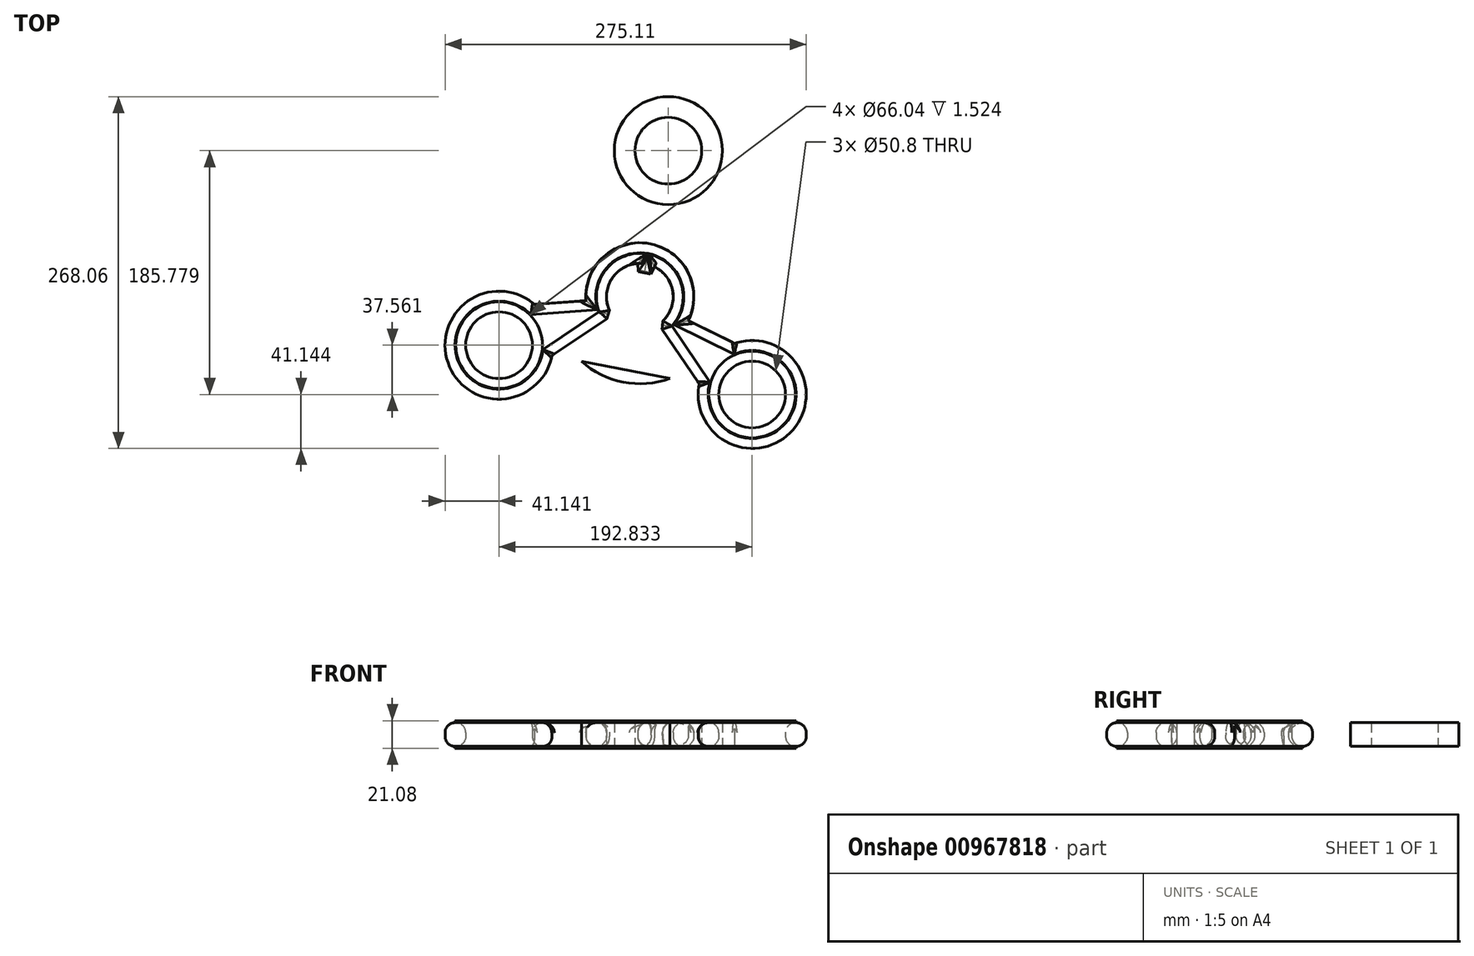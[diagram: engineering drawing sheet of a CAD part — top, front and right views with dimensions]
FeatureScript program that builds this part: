
annotation { "Feature Type Name" : "Feature", "Feature Type Description" : "" }
export const myFeature = defineFeature(function(context is Context, id is Id, definition is map)
    precondition{}
    {
        {
            var Q0;
            Q0=qCreatedBy(makeId("Top.planeOp"),FACE);
            var sketch = newSketch(context, id + "F0", { "sketchPlane" : qUnion([Q0])});
            skCircle(sketch, "E0", {"center": v(0, 0) * mm, "radius": 66.28 * mm});
            skLineSegment(sketch, "E1", {"start": v(0, 66.28) * mm, "end": v(0, -66.28) * mm});
            skCircle(sketch, "E2.cCircle", {"center": v(0, 0) * mm, "radius": 56.71 * mm, "construction": true});
            skLineSegment(sketch, "E2.0", {"start": v(-107.26, -36.89) * mm, "end": v(21.69, 111.33) * mm});
            skLineSegment(sketch, "E2.1", {"start": v(21.69, 111.33) * mm, "end": v(85.57, -74.45) * mm});
            skLineSegment(sketch, "E2.2", {"start": v(85.57, -74.45) * mm, "end": v(-107.26, -36.89) * mm});
            skPoint(sketch, "E2.0.midPoint", {"position": v(-42.79, 37.22) * mm});
            skCircle(sketch, "E3", {"center": v(-107.26, -36.89) * mm, "radius": 41.14 * mm});
            skCircle(sketch, "E4", {"center": v(85.57, -74.45) * mm, "radius": 41.14 * mm});
            skCircle(sketch, "E5", {"center": v(21.69, 111.33) * mm, "radius": 41.14 * mm});
            skCircle(sketch, "E6", {"center": v(0, 0) * mm, "radius": 41.15 * mm});
            skLineSegment(sketch, "E7", {"start": v(0, 0) * mm, "end": v(-5.32, 80.3) * mm});
            skLineSegment(sketch, "E8", {"start": v(-5.32, 80.3) * mm, "end": v(-80.26, -5.85) * mm});
            skLineSegment(sketch, "E9", {"start": v(21.69, 111.33) * mm, "end": v(53.63, 18.44) * mm});
            skLineSegment(sketch, "E10", {"start": v(35.06, 72.43) * mm, "end": v(0, 0) * mm});
            skCircle(sketch, "E11", {"center": v(-107.26, -36.89) * mm, "radius": 25.4 * mm});
            skCircle(sketch, "E12", {"center": v(21.69, 111.33) * mm, "radius": 25.4 * mm});
            skCircle(sketch, "E13", {"center": v(85.57, -74.45) * mm, "radius": 25.4 * mm});
            skLineSegment(sketch, "E14", {"start": v(0, 0) * mm, "end": v(-80.26, -5.85) * mm});
            skLineSegment(sketch, "E15", {"start": v(-66.88, -44.75) * mm, "end": v(0, 0) * mm});
            skLineSegment(sketch, "E16", {"start": v(0, 0) * mm, "end": v(45.2, -66.58) * mm});
            skLineSegment(sketch, "E17", {"start": v(0, 0) * mm, "end": v(72.2, -35.54) * mm});
            skLineSegment(sketch, "E18", {"start": v(-5.32, 80.3) * mm, "end": v(35.06, 72.43) * mm});
            skLineSegment(sketch, "E19", {"start": v(72.2, -35.54) * mm, "end": v(45.2, -66.58) * mm});
            skLineSegment(sketch, "E20", {"start": v(-80.26, -5.85) * mm, "end": v(-66.88, -44.75) * mm});
            skCircle(sketch, "E21", {"center": v(0, 0) * mm, "radius": 25.4 * mm});
            skSolve(sketch);
        }
        {
            var Q0;
            {var subQ0=sQuery(id+"F0.wireOp",EDGE,"E7");var subQ1=sQuery(id+"F0.wireOp",EDGE,"E6");var subQ2=makeQuery(id+"F0.imprint","INTERSECT",VERTEX,{"derivedFrom":[subQ1,subQ0]});Q0=makeQuery(id+"F0.imprint","IMPRINT",FACE,{"disambiguationData":[TD([[makeQuery(id+"F0.imprint","IMPRINT",EDGE,{"disambiguationData":[TD([[subQ2,-1.0]])],"derivedFrom":subQ1}),1.0]])]});}
            var Q1;
            {var subQ0=sQuery(id+"F0.wireOp",EDGE,"E6");var subQ1=sQuery(id+"F0.wireOp",EDGE,"E1");var subQ2=makeQuery(id+"F0.imprint","INTERSECT",VERTEX,{"disambiguationData":[OD(0.0)],"derivedFrom":[subQ1,subQ0]});Q1=makeQuery(id+"F0.imprint","IMPRINT",FACE,{"disambiguationData":[TD([[makeQuery(id+"F0.imprint","IMPRINT",EDGE,{"disambiguationData":[TD([[subQ2,-1.0]])],"derivedFrom":subQ1}),1.0]])]});}
            var Q2;
            {var subQ0=sQuery(id+"F0.wireOp",EDGE,"E10");var subQ1=sQuery(id+"F0.wireOp",EDGE,"E6");var subQ2=makeQuery(id+"F0.imprint","INTERSECT",VERTEX,{"derivedFrom":[subQ1,subQ0]});Q2=makeQuery(id+"F0.imprint","IMPRINT",FACE,{"disambiguationData":[TD([[makeQuery(id+"F0.imprint","IMPRINT",EDGE,{"disambiguationData":[TD([[subQ2,1.0]])],"derivedFrom":subQ1}),1.0]])]});}
            var Q3;
            {var subQ0=sQuery(id+"F0.wireOp",EDGE,"E6");var subQ1=sQuery(id+"F0.wireOp",EDGE,"E1");var subQ2=makeQuery(id+"F0.imprint","INTERSECT",VERTEX,{"disambiguationData":[OD(0.0)],"derivedFrom":[subQ1,subQ0]});Q3=makeQuery(id+"F0.imprint","IMPRINT",FACE,{"disambiguationData":[TD([[makeQuery(id+"F0.imprint","IMPRINT",EDGE,{"disambiguationData":[TD([[subQ2,-1.0]])],"derivedFrom":subQ1}),-1.0]])]});}
            var Q4;
            {var subQ0=sQuery(id+"F0.wireOp",EDGE,"E14");var subQ1=sQuery(id+"F0.wireOp",EDGE,"E6");var subQ2=makeQuery(id+"F0.imprint","INTERSECT",VERTEX,{"derivedFrom":[subQ1,subQ0]});Q4=makeQuery(id+"F0.imprint","IMPRINT",FACE,{"disambiguationData":[TD([[makeQuery(id+"F0.imprint","IMPRINT",EDGE,{"disambiguationData":[TD([[subQ2,-1.0]])],"derivedFrom":subQ1}),1.0]])]});}
            var Q5;
            {var subQ0=sQuery(id+"F0.wireOp",EDGE,"E21");var subQ1=sQuery(id+"F0.wireOp",EDGE,"E1");var subQ2=makeQuery(id+"F0.imprint","INTERSECT",VERTEX,{"disambiguationData":[OD(1.0)],"derivedFrom":[subQ1,subQ0]});Q5=makeQuery(id+"F0.imprint","IMPRINT",FACE,{"disambiguationData":[TD([[makeQuery(id+"F0.imprint","IMPRINT",EDGE,{"disambiguationData":[TD([[subQ2,-1.0]])],"derivedFrom":subQ1}),-1.0]])]});}
            var Q6;
            {var subQ0=sQuery(id+"F0.wireOp",EDGE,"E21");var subQ1=sQuery(id+"F0.wireOp",EDGE,"E1");var subQ2=makeQuery(id+"F0.imprint","INTERSECT",VERTEX,{"disambiguationData":[OD(1.0)],"derivedFrom":[subQ1,subQ0]});Q6=makeQuery(id+"F0.imprint","IMPRINT",FACE,{"disambiguationData":[TD([[makeQuery(id+"F0.imprint","IMPRINT",EDGE,{"disambiguationData":[TD([[subQ2,-1.0]])],"derivedFrom":subQ1}),1.0]])]});}
            var Q7;
            {var subQ0=sQuery(id+"F0.wireOp",EDGE,"E16");var subQ1=sQuery(id+"F0.wireOp",EDGE,"E6");var subQ2=makeQuery(id+"F0.imprint","INTERSECT",VERTEX,{"derivedFrom":[subQ1,subQ0]});Q7=makeQuery(id+"F0.imprint","IMPRINT",FACE,{"disambiguationData":[TD([[makeQuery(id+"F0.imprint","IMPRINT",EDGE,{"disambiguationData":[TD([[subQ2,-1.0]])],"derivedFrom":subQ1}),1.0]])]});}
            var Q8;
            {var subQ0=sQuery(id+"F0.wireOp",EDGE,"E16");var subQ1=sQuery(id+"F0.wireOp",EDGE,"E0");var subQ2=makeQuery(id+"F0.imprint","INTERSECT",VERTEX,{"derivedFrom":[subQ1,subQ0]});Q8=makeQuery(id+"F0.imprint","IMPRINT",FACE,{"disambiguationData":[TD([[makeQuery(id+"F0.imprint","IMPRINT",EDGE,{"disambiguationData":[TD([[subQ2,-1.0]])],"derivedFrom":subQ1}),1.0]])]});}
            var Q9;
            {var subQ0=sQuery(id+"F0.wireOp",EDGE,"E14");var subQ1=sQuery(id+"F0.wireOp",EDGE,"E0");var subQ2=makeQuery(id+"F0.imprint","INTERSECT",VERTEX,{"derivedFrom":[subQ1,subQ0]});Q9=makeQuery(id+"F0.imprint","IMPRINT",FACE,{"disambiguationData":[TD([[makeQuery(id+"F0.imprint","IMPRINT",EDGE,{"disambiguationData":[TD([[subQ2,-1.0]])],"derivedFrom":subQ1}),1.0]])]});}
            var Q10;
            {var subQ0=sQuery(id+"F0.wireOp",EDGE,"E14");var subQ1=sQuery(id+"F0.wireOp",EDGE,"E0");var subQ2=makeQuery(id+"F0.imprint","INTERSECT",VERTEX,{"derivedFrom":[subQ1,subQ0]});Q10=makeQuery(id+"F0.imprint","IMPRINT",FACE,{"disambiguationData":[TD([[makeQuery(id+"F0.imprint","IMPRINT",EDGE,{"disambiguationData":[TD([[subQ2,-1.0]])],"derivedFrom":subQ1}),-1.0]])]});}
            var Q11;
            {var subQ0=sQuery(id+"F0.wireOp",EDGE,"E20");Q11=makeQuery(id+"F0.imprint","IMPRINT",FACE,{"disambiguationData":[TD([[makeQuery(id+"F0.imprint","IMPRINT",EDGE,{"derivedFrom":subQ0}),-1.0]])]});}
            var Q12;
            {var subQ0=sQuery(id+"F0.wireOp",EDGE,"E20");Q12=makeQuery(id+"F0.imprint","IMPRINT",FACE,{"disambiguationData":[TD([[makeQuery(id+"F0.imprint","IMPRINT",EDGE,{"derivedFrom":subQ0}),1.0]])]});}
            var Q13;
            {var subQ2=sQuery(id+"F0.wireOp",EDGE,"E2.0");var subQ4=sQuery(id+"F0.wireOp",EDGE,"E11");var subQ5=makeQuery(id+"F0.imprint","INTERSECT",VERTEX,{"derivedFrom":[subQ2,subQ4]});Q13=makeQuery(id+"F0.imprint","IMPRINT",FACE,{"disambiguationData":[TD([[makeQuery(id+"F0.imprint","IMPRINT",EDGE,{"disambiguationData":[TD([[subQ5,-1.0]])],"derivedFrom":subQ4}),-1.0]])]});}
            var Q14;
            {var subQ0=sQuery(id+"F0.wireOp",EDGE,"E19");Q14=makeQuery(id+"F0.imprint","IMPRINT",FACE,{"disambiguationData":[TD([[makeQuery(id+"F0.imprint","IMPRINT",EDGE,{"derivedFrom":subQ0}),1.0]])]});}
            var Q15;
            {var subQ0=sQuery(id+"F0.wireOp",EDGE,"E16");var subQ1=sQuery(id+"F0.wireOp",EDGE,"E0");var subQ2=makeQuery(id+"F0.imprint","INTERSECT",VERTEX,{"derivedFrom":[subQ1,subQ0]});Q15=makeQuery(id+"F0.imprint","IMPRINT",FACE,{"disambiguationData":[TD([[makeQuery(id+"F0.imprint","IMPRINT",EDGE,{"disambiguationData":[TD([[subQ2,-1.0]])],"derivedFrom":subQ1}),-1.0]])]});}
            var Q16;
            {var subQ2=sQuery(id+"F0.wireOp",EDGE,"E2.1");var subQ4=sQuery(id+"F0.wireOp",EDGE,"E13");var subQ5=makeQuery(id+"F0.imprint","INTERSECT",VERTEX,{"derivedFrom":[subQ2,subQ4]});Q16=makeQuery(id+"F0.imprint","IMPRINT",FACE,{"disambiguationData":[TD([[makeQuery(id+"F0.imprint","IMPRINT",EDGE,{"disambiguationData":[TD([[subQ5,1.0]])],"derivedFrom":subQ4}),-1.0]])]});}
            var Q17;
            {var subQ0=sQuery(id+"F0.wireOp",EDGE,"E19");Q17=makeQuery(id+"F0.imprint","IMPRINT",FACE,{"disambiguationData":[TD([[makeQuery(id+"F0.imprint","IMPRINT",EDGE,{"derivedFrom":subQ0}),-1.0]])]});}
            var Q18;
            {var subQ0=sQuery(id+"F0.wireOp",EDGE,"E1");var subQ1=sQuery(id+"F0.wireOp",EDGE,"E0");var subQ2=makeQuery(id+"F0.imprint","INTERSECT",VERTEX,{"disambiguationData":[OD(0.0)],"derivedFrom":[subQ1,subQ0]});Q18=makeQuery(id+"F0.imprint","IMPRINT",FACE,{"disambiguationData":[TD([[makeQuery(id+"F0.imprint","IMPRINT",EDGE,{"disambiguationData":[TD([[subQ2,1.0]])],"derivedFrom":subQ1}),1.0]])]});}
            var Q19;
            {var subQ0=sQuery(id+"F0.wireOp",EDGE,"E1");var subQ1=sQuery(id+"F0.wireOp",EDGE,"E0");var subQ2=makeQuery(id+"F0.imprint","INTERSECT",VERTEX,{"disambiguationData":[OD(0.0)],"derivedFrom":[subQ1,subQ0]});Q19=makeQuery(id+"F0.imprint","IMPRINT",FACE,{"disambiguationData":[TD([[makeQuery(id+"F0.imprint","IMPRINT",EDGE,{"disambiguationData":[TD([[subQ2,-1.0]])],"derivedFrom":subQ1}),1.0]])]});}
            var Q20;
            {var subQ4=sQuery(id+"F0.wireOp",EDGE,"E0");var subQ6=makeQuery(id+"F0.imprint","INTERSECT",VERTEX,{"disambiguationData":[OD(0.0)],"derivedFrom":[subQ4,sQuery(id+"F0.wireOp",EDGE,"E1")]});Q20=makeQuery(id+"F0.imprint","IMPRINT",FACE,{"disambiguationData":[TD([[makeQuery(id+"F0.imprint","IMPRINT",EDGE,{"disambiguationData":[TD([[subQ6,1.0]])],"derivedFrom":subQ4}),-1.0]])]});}
            var Q21;
            {var subQ0=sQuery(id+"F0.wireOp",EDGE,"E18");Q21=makeQuery(id+"F0.imprint","IMPRINT",FACE,{"disambiguationData":[TD([[makeQuery(id+"F0.imprint","IMPRINT",EDGE,{"derivedFrom":subQ0}),-1.0]])]});}
            var Q22;
            {var subQ2=sQuery(id+"F0.wireOp",EDGE,"E2.0");var subQ4=sQuery(id+"F0.wireOp",EDGE,"E12");var subQ5=makeQuery(id+"F0.imprint","INTERSECT",VERTEX,{"derivedFrom":[subQ2,subQ4]});Q22=makeQuery(id+"F0.imprint","IMPRINT",FACE,{"disambiguationData":[TD([[makeQuery(id+"F0.imprint","IMPRINT",EDGE,{"disambiguationData":[TD([[subQ5,1.0]])],"derivedFrom":subQ4}),-1.0]])]});}
            var Q23;
            {var subQ0=sQuery(id+"F0.wireOp",EDGE,"E18");Q23=makeQuery(id+"F0.imprint","IMPRINT",FACE,{"disambiguationData":[TD([[makeQuery(id+"F0.imprint","IMPRINT",EDGE,{"derivedFrom":subQ0}),1.0]])]});}
            extrude(context, id + "F1", {"entities" : qUnion([Q0, Q1, Q2, Q3, Q4, Q5, Q6, Q7, Q8, Q9, Q10, Q11, Q12, Q13, Q14, Q15, Q16, Q17, Q18, Q19, Q20, Q21, Q22, Q23]), "depth" : 18.03 * mm, "offsetDistance" : 25.4 * mm});
        }
        {
            var Q0;
            Q0=makeQuery(id+"F1.opExtrude","CAP_EDGE",EDGE,{"disambiguationData":[OSD([sQuery(id+"F0.wireOp",EDGE,"E4")])],"isStart":false});
            var Q1;
            Q1=makeQuery(id+"F1.opExtrude","CAP_FACE",FACE,{"disambiguationData":[OSD([sQuery(id+"F0.wireOp",EDGE,"E3"),sQuery(id+"F0.wireOp",EDGE,"E4"),sQuery(id+"F0.wireOp",EDGE,"E5"),sQuery(id+"F0.wireOp",EDGE,"E6"),sQuery(id+"F0.wireOp",EDGE,"E7"),sQuery(id+"F0.wireOp",EDGE,"E10"),sQuery(id+"F0.wireOp",EDGE,"E11"),sQuery(id+"F0.wireOp",EDGE,"E12"),sQuery(id+"F0.wireOp",EDGE,"E13"),sQuery(id+"F0.wireOp",EDGE,"E14"),sQuery(id+"F0.wireOp",EDGE,"E15"),sQuery(id+"F0.wireOp",EDGE,"E16"),sQuery(id+"F0.wireOp",EDGE,"E17"),sQuery(id+"F0.wireOp",EDGE,"E21")])],"isStart":false});
            fillet(context, id + "F2", {"entities" : qUnion([Q0, Q1]), "radius" : 7.62 * mm, "tangentPropagation" : true, "allowEdgeOverflow" : false});
        }
        {
            var Q0;
            Q0=makeQuery(id+"F1.opExtrude","CAP_FACE",FACE,{"disambiguationData":[OSD([sQuery(id+"F0.wireOp",EDGE,"E3"),sQuery(id+"F0.wireOp",EDGE,"E4"),sQuery(id+"F0.wireOp",EDGE,"E5"),sQuery(id+"F0.wireOp",EDGE,"E6"),sQuery(id+"F0.wireOp",EDGE,"E7"),sQuery(id+"F0.wireOp",EDGE,"E10"),sQuery(id+"F0.wireOp",EDGE,"E11"),sQuery(id+"F0.wireOp",EDGE,"E12"),sQuery(id+"F0.wireOp",EDGE,"E13"),sQuery(id+"F0.wireOp",EDGE,"E14"),sQuery(id+"F0.wireOp",EDGE,"E15"),sQuery(id+"F0.wireOp",EDGE,"E16"),sQuery(id+"F0.wireOp",EDGE,"E17"),sQuery(id+"F0.wireOp",EDGE,"E21")])],"isStart":true});
            fillet(context, id + "F3", {"entities" : qUnion([Q0]), "radius" : 7.62 * mm, "tangentPropagation" : true, "allowEdgeOverflow" : false});
        }
        {
            var Q0;
            {var subQ0=sQuery(id+"F0.wireOp",EDGE,"E16");var subQ1=sQuery(id+"F0.wireOp",EDGE,"E15");var subQ2=sQuery(id+"F0.wireOp",EDGE,"E6");var subQ3=makeQuery(id+"F0.imprint","INTERSECT",VERTEX,{"disambiguationData":[OD(1.0)],"derivedFrom":[sQuery(id+"F0.wireOp",EDGE,"E1"),subQ2]});Q0=makeQuery(id+"F2.opFillet","BLEND_EDGE",EDGE,{"blendedFrom":[makeQuery(id+"F1.opExtrude","CAP_EDGE",EDGE,{"disambiguationData":[OSD([subQ2]),TDD([makeQuery(id+"F0.imprint","IMPRINT",EDGE,{"disambiguationData":[TD([[subQ3,1.0]])],"derivedFrom":subQ2}),makeQuery(id+"F0.imprint","IMPRINT",EDGE,{"disambiguationData":[TD([[subQ3,-1.0]])],"derivedFrom":subQ2})])],"isStart":false}),makeQuery(id+"F1.opExtrude","CAP_FACE",FACE,{"disambiguationData":[OSD([sQuery(id+"F0.wireOp",EDGE,"E3"),sQuery(id+"F0.wireOp",EDGE,"E4"),sQuery(id+"F0.wireOp",EDGE,"E5"),subQ2,sQuery(id+"F0.wireOp",EDGE,"E7"),sQuery(id+"F0.wireOp",EDGE,"E10"),sQuery(id+"F0.wireOp",EDGE,"E11"),sQuery(id+"F0.wireOp",EDGE,"E12"),sQuery(id+"F0.wireOp",EDGE,"E13"),sQuery(id+"F0.wireOp",EDGE,"E14"),subQ1,subQ0,sQuery(id+"F0.wireOp",EDGE,"E17"),sQuery(id+"F0.wireOp",EDGE,"E21")])],"isStart":false})],"blendedInto":[makeQuery(id+"F1.opExtrude","CAP_FACE",FACE,{"disambiguationData":[OSD([sQuery(id+"F0.wireOp",EDGE,"E3"),sQuery(id+"F0.wireOp",EDGE,"E4"),sQuery(id+"F0.wireOp",EDGE,"E5"),subQ2,sQuery(id+"F0.wireOp",EDGE,"E7"),sQuery(id+"F0.wireOp",EDGE,"E10"),sQuery(id+"F0.wireOp",EDGE,"E11"),sQuery(id+"F0.wireOp",EDGE,"E12"),sQuery(id+"F0.wireOp",EDGE,"E13"),sQuery(id+"F0.wireOp",EDGE,"E14"),subQ1,subQ0,sQuery(id+"F0.wireOp",EDGE,"E17"),sQuery(id+"F0.wireOp",EDGE,"E21")])],"isStart":false})]});}
            var Q1;
            Q1=makeQuery(id+"F2.opFillet","BLEND_FACE",FACE,{"disambiguationData":[OSD([sQuery(id+"F0.wireOp",EDGE,"E15")])]});
            var Q2;
            {var subQ0=sQuery(id+"F0.wireOp",EDGE,"E6");var subQ1=makeQuery(id+"F0.imprint","INTERSECT",VERTEX,{"disambiguationData":[OD(1.0)],"derivedFrom":[sQuery(id+"F0.wireOp",EDGE,"E1"),subQ0]});Q2=makeQuery(id+"F2.opFillet","BLEND_FACE",FACE,{"disambiguationData":[OSD([subQ0]),TDD([makeQuery(id+"F1.opExtrude","CAP_EDGE",EDGE,{"disambiguationData":[OSD([subQ0]),TDD([makeQuery(id+"F0.imprint","IMPRINT",EDGE,{"disambiguationData":[TD([[subQ1,1.0]])],"derivedFrom":subQ0}),makeQuery(id+"F0.imprint","IMPRINT",EDGE,{"disambiguationData":[TD([[subQ1,-1.0]])],"derivedFrom":subQ0})])],"isStart":false})])]});}
            var Q3;
            {var subQ0=sQuery(id+"F0.wireOp",EDGE,"E6");Q3=makeQuery(id+"F2.opFillet","BLEND_FACE",FACE,{"disambiguationData":[OSD([subQ0]),TDD([makeQuery(id+"F1.opExtrude","CAP_EDGE",EDGE,{"disambiguationData":[OSD([subQ0]),TDD([makeQuery(id+"F0.imprint","IMPRINT",EDGE,{"disambiguationData":[TD([[makeQuery(id+"F0.imprint","INTERSECT",VERTEX,{"derivedFrom":[subQ0,sQuery(id+"F0.wireOp",EDGE,"E10")]}),1.0]])],"derivedFrom":subQ0})])],"isStart":false})])]});}
            var Q4;
            Q4=makeQuery(id+"F2.opFillet","BLEND_FACE",FACE,{"disambiguationData":[OSD([sQuery(id+"F0.wireOp",EDGE,"E17")])]});
            var Q5;
            {var subQ0=sQuery(id+"F0.wireOp",EDGE,"E16");Q5=makeQuery(id+"F2.opFillet","BLEND_EDGE",EDGE,{"blendedFrom":[makeQuery(id+"F1.opExtrude","CAP_EDGE",EDGE,{"disambiguationData":[OSD([subQ0])],"isStart":false}),makeQuery(id+"F1.opExtrude","CAP_FACE",FACE,{"disambiguationData":[OSD([sQuery(id+"F0.wireOp",EDGE,"E3"),sQuery(id+"F0.wireOp",EDGE,"E4"),sQuery(id+"F0.wireOp",EDGE,"E5"),sQuery(id+"F0.wireOp",EDGE,"E6"),sQuery(id+"F0.wireOp",EDGE,"E7"),sQuery(id+"F0.wireOp",EDGE,"E10"),sQuery(id+"F0.wireOp",EDGE,"E11"),sQuery(id+"F0.wireOp",EDGE,"E12"),sQuery(id+"F0.wireOp",EDGE,"E13"),sQuery(id+"F0.wireOp",EDGE,"E14"),sQuery(id+"F0.wireOp",EDGE,"E15"),subQ0,sQuery(id+"F0.wireOp",EDGE,"E17"),sQuery(id+"F0.wireOp",EDGE,"E21")])],"isStart":false})],"blendedInto":[makeQuery(id+"F1.opExtrude","CAP_FACE",FACE,{"disambiguationData":[OSD([sQuery(id+"F0.wireOp",EDGE,"E3"),sQuery(id+"F0.wireOp",EDGE,"E4"),sQuery(id+"F0.wireOp",EDGE,"E5"),sQuery(id+"F0.wireOp",EDGE,"E6"),sQuery(id+"F0.wireOp",EDGE,"E7"),sQuery(id+"F0.wireOp",EDGE,"E10"),sQuery(id+"F0.wireOp",EDGE,"E11"),sQuery(id+"F0.wireOp",EDGE,"E12"),sQuery(id+"F0.wireOp",EDGE,"E13"),sQuery(id+"F0.wireOp",EDGE,"E14"),sQuery(id+"F0.wireOp",EDGE,"E15"),subQ0,sQuery(id+"F0.wireOp",EDGE,"E17"),sQuery(id+"F0.wireOp",EDGE,"E21")])],"isStart":false})]});}
            var Q6;
            Q6=makeQuery(id+"F2.opFillet","BLEND_FACE",FACE,{"disambiguationData":[OSD([sQuery(id+"F0.wireOp",EDGE,"E16")])]});
            var Q7;
            {var subQ0=sQuery(id+"F0.wireOp",EDGE,"E21");Q7=makeQuery(id+"F2.opFillet","BLEND_EDGE",EDGE,{"blendedFrom":[makeQuery(id+"F1.opExtrude","CAP_EDGE",EDGE,{"disambiguationData":[OSD([subQ0])],"isStart":false}),makeQuery(id+"F1.opExtrude","CAP_FACE",FACE,{"disambiguationData":[OSD([sQuery(id+"F0.wireOp",EDGE,"E3"),sQuery(id+"F0.wireOp",EDGE,"E4"),sQuery(id+"F0.wireOp",EDGE,"E5"),sQuery(id+"F0.wireOp",EDGE,"E6"),sQuery(id+"F0.wireOp",EDGE,"E7"),sQuery(id+"F0.wireOp",EDGE,"E10"),sQuery(id+"F0.wireOp",EDGE,"E11"),sQuery(id+"F0.wireOp",EDGE,"E12"),sQuery(id+"F0.wireOp",EDGE,"E13"),sQuery(id+"F0.wireOp",EDGE,"E14"),sQuery(id+"F0.wireOp",EDGE,"E15"),sQuery(id+"F0.wireOp",EDGE,"E16"),sQuery(id+"F0.wireOp",EDGE,"E17"),subQ0])],"isStart":false})],"blendedInto":[makeQuery(id+"F1.opExtrude","CAP_FACE",FACE,{"disambiguationData":[OSD([sQuery(id+"F0.wireOp",EDGE,"E3"),sQuery(id+"F0.wireOp",EDGE,"E4"),sQuery(id+"F0.wireOp",EDGE,"E5"),sQuery(id+"F0.wireOp",EDGE,"E6"),sQuery(id+"F0.wireOp",EDGE,"E7"),sQuery(id+"F0.wireOp",EDGE,"E10"),sQuery(id+"F0.wireOp",EDGE,"E11"),sQuery(id+"F0.wireOp",EDGE,"E12"),sQuery(id+"F0.wireOp",EDGE,"E13"),sQuery(id+"F0.wireOp",EDGE,"E14"),sQuery(id+"F0.wireOp",EDGE,"E15"),sQuery(id+"F0.wireOp",EDGE,"E16"),sQuery(id+"F0.wireOp",EDGE,"E17"),subQ0])],"isStart":false})]});}
            var Q8;
            {var subQ0=sQuery(id+"F0.wireOp",EDGE,"E6");Q8=makeQuery(id+"F2.opFillet","BLEND_FACE",FACE,{"disambiguationData":[OSD([subQ0]),TDD([makeQuery(id+"F1.opExtrude","CAP_EDGE",EDGE,{"disambiguationData":[OSD([subQ0]),TDD([makeQuery(id+"F0.imprint","IMPRINT",EDGE,{"disambiguationData":[TD([[makeQuery(id+"F0.imprint","INTERSECT",VERTEX,{"derivedFrom":[subQ0,sQuery(id+"F0.wireOp",EDGE,"E7")]}),-1.0]])],"derivedFrom":subQ0})])],"isStart":false})])]});}
            var Q9;
            Q9=makeQuery(id+"F2.opFillet","BLEND_FACE",FACE,{"disambiguationData":[OSD([sQuery(id+"F0.wireOp",EDGE,"E14")])]});
            var Q10;
            Q10=makeQuery(id+"F2.opFillet","BLEND_FACE",FACE,{"disambiguationData":[OSD([sQuery(id+"F0.wireOp",EDGE,"E10")])]});
            var Q11;
            Q11=makeQuery(id+"F2.opFillet","BLEND_FACE",FACE,{"disambiguationData":[OSD([sQuery(id+"F0.wireOp",EDGE,"E7")])]});
            var Q12;
            Q12=makeQuery(id+"F2.opFillet","BLEND_FACE",FACE,{"disambiguationData":[OSD([sQuery(id+"F0.wireOp",EDGE,"E3")])]});
            var Q13;
            Q13=makeQuery(id+"F2.opFillet","BLEND_FACE",FACE,{"disambiguationData":[OSD([sQuery(id+"F0.wireOp",EDGE,"E5")])]});
            chamfer(context, id + "F4", {"entities" : qUnion([Q0, Q1, Q2, Q3, Q4, Q5, Q6, Q7, Q8, Q9, Q10, Q11, Q12, Q13]), "width" : 5.08 * mm, "tangentPropagation" : true});
        }
        {
            var Q0;
            Q0=makeQuery(id+"F1.opExtrude","CAP_FACE",FACE,{"disambiguationData":[OSD([sQuery(id+"F0.wireOp",EDGE,"E3"),sQuery(id+"F0.wireOp",EDGE,"E4"),sQuery(id+"F0.wireOp",EDGE,"E5"),sQuery(id+"F0.wireOp",EDGE,"E6"),sQuery(id+"F0.wireOp",EDGE,"E7"),sQuery(id+"F0.wireOp",EDGE,"E10"),sQuery(id+"F0.wireOp",EDGE,"E11"),sQuery(id+"F0.wireOp",EDGE,"E12"),sQuery(id+"F0.wireOp",EDGE,"E13"),sQuery(id+"F0.wireOp",EDGE,"E14"),sQuery(id+"F0.wireOp",EDGE,"E15"),sQuery(id+"F0.wireOp",EDGE,"E16"),sQuery(id+"F0.wireOp",EDGE,"E17"),sQuery(id+"F0.wireOp",EDGE,"E21")])],"isStart":false});
            extrude(context, id + "F5", {"entities" : qUnion([Q0]), "operationType" : NewBodyOperationType.ADD, "depth" : 1.52 * mm, "offsetDistance" : 25.4 * mm});
        }
        {
            var Q0;
            Q0=makeQuery(id+"F1.opExtrude","CAP_FACE",FACE,{"disambiguationData":[OSD([sQuery(id+"F0.wireOp",EDGE,"E3"),sQuery(id+"F0.wireOp",EDGE,"E4"),sQuery(id+"F0.wireOp",EDGE,"E5"),sQuery(id+"F0.wireOp",EDGE,"E6"),sQuery(id+"F0.wireOp",EDGE,"E7"),sQuery(id+"F0.wireOp",EDGE,"E10"),sQuery(id+"F0.wireOp",EDGE,"E11"),sQuery(id+"F0.wireOp",EDGE,"E12"),sQuery(id+"F0.wireOp",EDGE,"E13"),sQuery(id+"F0.wireOp",EDGE,"E14"),sQuery(id+"F0.wireOp",EDGE,"E15"),sQuery(id+"F0.wireOp",EDGE,"E16"),sQuery(id+"F0.wireOp",EDGE,"E17"),sQuery(id+"F0.wireOp",EDGE,"E21")])],"isStart":true});
            extrude(context, id + "F6", {"entities" : qUnion([Q0]), "operationType" : NewBodyOperationType.ADD, "depth" : 1.52 * mm, "offsetDistance" : 25.4 * mm});
        }
    });
